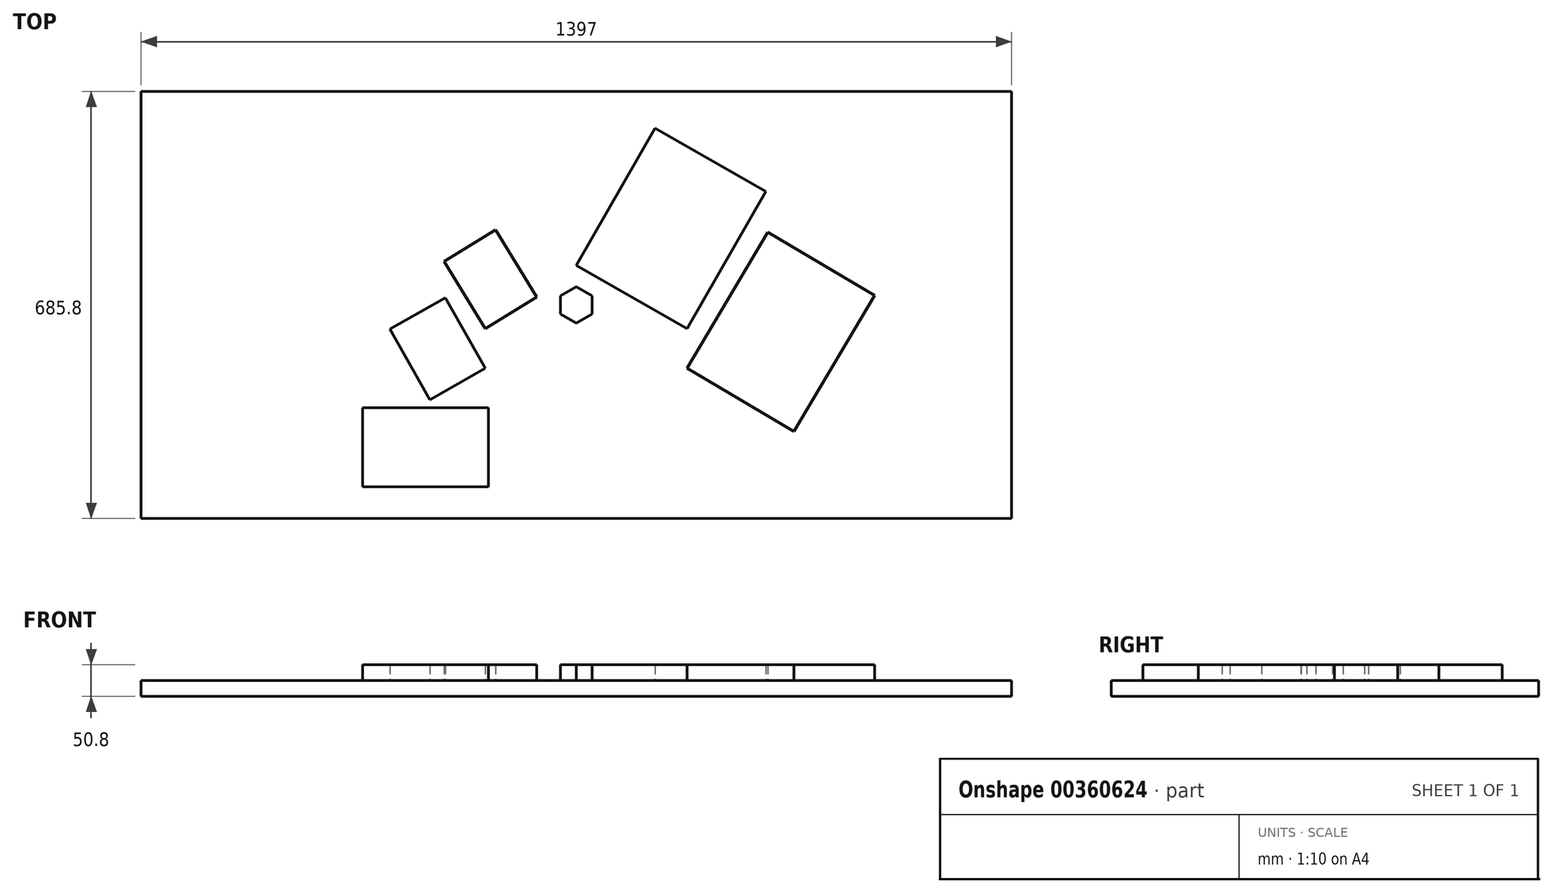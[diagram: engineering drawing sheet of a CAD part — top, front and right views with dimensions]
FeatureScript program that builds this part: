
annotation { "Feature Type Name" : "Feature", "Feature Type Description" : "" }
export const myFeature = defineFeature(function(context is Context, id is Id, definition is map)
    precondition{}
    {
        {
            var Q0;
            Q0=qCreatedBy(makeId("Top.planeOp"),FACE);
            var sketch = newSketch(context, id + "F0", { "sketchPlane" : qUnion([Q0])});
            skLineSegment(sketch, "E0.bottom", {"start": v(698.5, 342.9) * mm, "end": v(-698.5, 342.9) * mm});
            skLineSegment(sketch, "E0.top", {"start": v(698.5, -342.9) * mm, "end": v(-698.5, -342.9) * mm});
            skLineSegment(sketch, "E0.left", {"start": v(698.5, 342.9) * mm, "end": v(698.5, -342.9) * mm});
            skLineSegment(sketch, "E0.right", {"start": v(-698.5, 342.9) * mm, "end": v(-698.5, -342.9) * mm});
            skPoint(sketch, "E0.middle", {"position": v(0, 0) * mm});
            skSolve(sketch);
        }
        {
            var Q0;
            Q0 = qSketchRegion(id + "F0", true);
            extrude(context, id + "F1", {"entities" : qUnion([Q0]), "depth" : 25.4 * mm});
        }
        {
            var Q0;
            Q0=makeQuery(id+"F1.opExtrude","CAP_FACE",FACE,{"disambiguationData":[OSD([sQuery(id+"F0.wireOp",EDGE,"E0.bottom"),sQuery(id+"F0.wireOp",EDGE,"E0.top"),sQuery(id+"F0.wireOp",EDGE,"E0.left"),sQuery(id+"F0.wireOp",EDGE,"E0.right")])],"isStart":false});
            var sketch = newSketch(context, id + "F2", { "sketchPlane" : qUnion([Q0])});
            skLineSegment(sketch, "E1.bottom", {"start": v(-120.65, -152.4) * mm, "end": v(120.65, -152.4) * mm, "construction": true});
            skLineSegment(sketch, "E1.top", {"start": v(-120.65, -50.8) * mm, "end": v(120.65, -50.8) * mm, "construction": true});
            skLineSegment(sketch, "E1.left", {"start": v(-120.65, -152.4) * mm, "end": v(-120.65, -50.8) * mm, "construction": true});
            skLineSegment(sketch, "E1.right", {"start": v(120.65, -152.4) * mm, "end": v(120.65, -50.8) * mm, "construction": true});
            skCircle(sketch, "E2.cCircle", {"center": v(0, 0) * mm, "radius": 25.4 * mm, "construction": true});
            skLineSegment(sketch, "E2.0", {"start": v(25.4, 14.66) * mm, "end": v(25.4, -14.66) * mm});
            skLineSegment(sketch, "E2.1", {"start": v(25.4, -14.66) * mm, "end": v(0, -29.33) * mm});
            skLineSegment(sketch, "E2.2", {"start": v(0, -29.33) * mm, "end": v(-25.4, -14.66) * mm});
            skLineSegment(sketch, "E2.3", {"start": v(-25.4, -14.66) * mm, "end": v(-25.4, 14.66) * mm});
            skLineSegment(sketch, "E2.4", {"start": v(-25.4, 14.66) * mm, "end": v(0, 29.33) * mm});
            skLineSegment(sketch, "E2.5", {"start": v(0, 29.33) * mm, "end": v(25.4, 14.66) * mm});
            skPoint(sketch, "E2.0.midPoint", {"position": v(25.4, 0) * mm});
            skPoint(sketch, "E3.endSnap0", {"position": v(0, 342.9) * mm});
            skPoint(sketch, "E4", {"position": v(0, -50.8) * mm});
            skLineSegment(sketch, "E5.bottom", {"start": v(177.8, -101.6) * mm, "end": v(349.25, -203.2) * mm});
            skLineSegment(sketch, "E5.top", {"start": v(307.29, 116.91) * mm, "end": v(478.74, 15.31) * mm});
            skLineSegment(sketch, "E5.left", {"start": v(177.8, -101.6) * mm, "end": v(307.29, 116.91) * mm});
            skLineSegment(sketch, "E5.right", {"start": v(349.25, -203.2) * mm, "end": v(478.74, 15.31) * mm});
            skPoint(sketch, "E6", {"position": v(263.52, -152.4) * mm});
            skPoint(sketch, "E7", {"position": v(120.65, -101.6) * mm});
            skLineSegment(sketch, "E8.bottom", {"start": v(0, 63.5) * mm, "end": v(177.8, -38.1) * mm});
            skLineSegment(sketch, "E8.top", {"start": v(126.02, 284.03) * mm, "end": v(303.82, 182.43) * mm});
            skLineSegment(sketch, "E8.left", {"start": v(0, 63.5) * mm, "end": v(126.02, 284.03) * mm});
            skLineSegment(sketch, "E8.right", {"start": v(177.8, -38.1) * mm, "end": v(303.82, 182.43) * mm});
            skPoint(sketch, "E9", {"position": v(88.9, 12.7) * mm});
            skLineSegment(sketch, "E10.bottom", {"start": v(-146.05, -38.1) * mm, "end": v(-63.5, 12.7) * mm});
            skLineSegment(sketch, "E10.top", {"start": v(-212.48, 69.85) * mm, "end": v(-129.93, 120.65) * mm});
            skLineSegment(sketch, "E10.left", {"start": v(-146.05, -38.1) * mm, "end": v(-212.48, 69.85) * mm});
            skLineSegment(sketch, "E10.right", {"start": v(-63.5, 12.7) * mm, "end": v(-129.93, 120.65) * mm});
            skPoint(sketch, "E11", {"position": v(-104.78, -12.7) * mm});
            skLineSegment(sketch, "E12.bottom", {"start": v(-234.95, -152.4) * mm, "end": v(-146.05, -101.8) * mm});
            skLineSegment(sketch, "E12.top", {"start": v(-299.5, -38.97) * mm, "end": v(-210.6, 11.62) * mm});
            skLineSegment(sketch, "E12.left", {"start": v(-234.95, -152.4) * mm, "end": v(-299.5, -38.97) * mm});
            skLineSegment(sketch, "E12.right", {"start": v(-146.05, -101.8) * mm, "end": v(-210.6, 11.62) * mm});
            skPoint(sketch, "E13", {"position": v(-190.5, -127.1) * mm});
            skLineSegment(sketch, "E14.bottom", {"start": v(-141.23, -292.1) * mm, "end": v(-141.23, -165.1) * mm});
            skLineSegment(sketch, "E14.top", {"start": v(-342.9, -292.1) * mm, "end": v(-342.9, -165.1) * mm});
            skLineSegment(sketch, "E14.left", {"start": v(-141.23, -292.1) * mm, "end": v(-342.9, -292.1) * mm});
            skLineSegment(sketch, "E14.right", {"start": v(-141.23, -165.1) * mm, "end": v(-342.9, -165.1) * mm});
            skPoint(sketch, "E15", {"position": v(-141.23, -228.6) * mm});
            skSolve(sketch);
        }
        {
            var Q0;
            Q0 = qSketchRegion(id + "F2", true);
            extrude(context, id + "F3", {"entities" : qUnion([Q0]), "depth" : 25.4 * mm});
        }
    });
